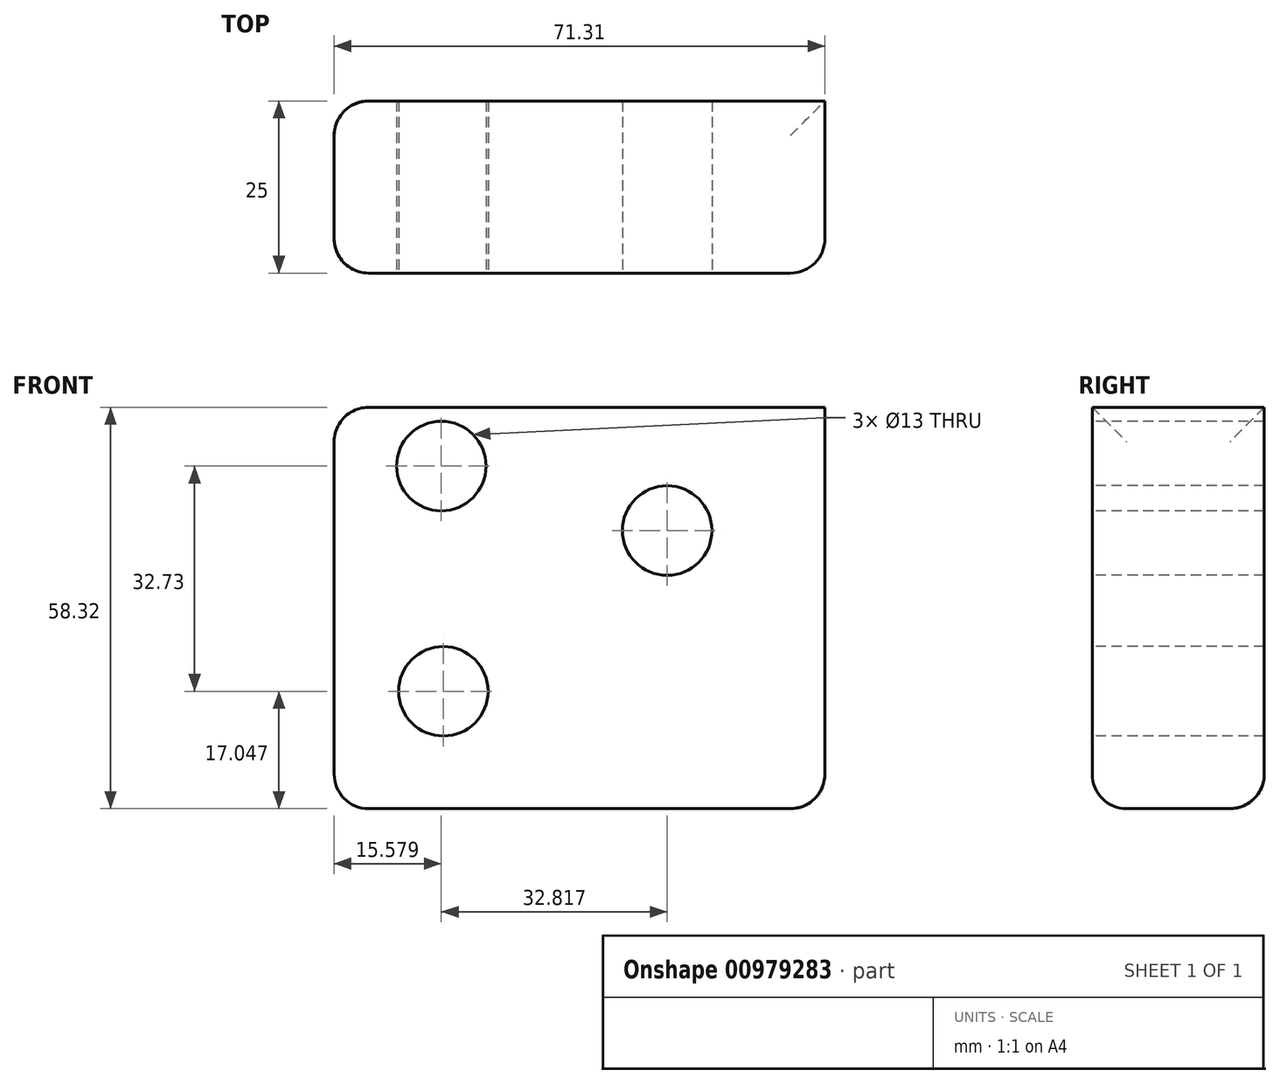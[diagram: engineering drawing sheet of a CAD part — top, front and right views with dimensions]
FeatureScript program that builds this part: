
annotation { "Feature Type Name" : "Feature", "Feature Type Description" : "" }
export const myFeature = defineFeature(function(context is Context, id is Id, definition is map)
    precondition{}
    {
        {
            var Q0;
            Q0=qCreatedBy(makeId("Front.planeOp"),FACE);
            var sketch = newSketch(context, id + "F0", { "sketchPlane" : qUnion([Q0])});
            skLineSegment(sketch, "E0.bottom", {"start": v(-136.04, 36.86) * mm, "end": v(-64.73, 36.86) * mm});
            skLineSegment(sketch, "E0.top", {"start": v(-136.04, -21.46) * mm, "end": v(-64.73, -21.46) * mm});
            skLineSegment(sketch, "E0.left", {"start": v(-136.04, 36.86) * mm, "end": v(-136.04, -21.46) * mm});
            skLineSegment(sketch, "E0.right", {"start": v(-64.73, 36.86) * mm, "end": v(-64.73, -21.46) * mm});
            skSolve(sketch);
        }
        {
            var Q0;
            Q0 = qSketchRegion(id + "F0", true);
            extrude(context, id + "F1", {"entities" : qUnion([Q0]), "depth" : 25 * mm, "offsetDistance" : 25 * mm});
        }
        {
            var Q0;
            Q0=makeQuery(id+"F1.opExtrude","CAP_FACE",FACE,{"disambiguationData":[OSD([sQuery(id+"F0.wireOp",EDGE,"E0.bottom"),sQuery(id+"F0.wireOp",EDGE,"E0.top"),sQuery(id+"F0.wireOp",EDGE,"E0.left"),sQuery(id+"F0.wireOp",EDGE,"E0.right")])],"isStart":false});
            var sketch = newSketch(context, id + "F2", { "sketchPlane" : qUnion([Q0])});
            skPoint(sketch, "E1", {"position": v(-120.46, 28.32) * mm});
            skPoint(sketch, "E2", {"position": v(-120.16, -4.41) * mm});
            skPoint(sketch, "E3", {"position": v(-87.64, 18.95) * mm});
            skSolve(sketch);
        }
        {
            var Q0;
            Q0=sQuery(id+"F2.wireOp",VERTEX,"E1");
            var Q1;
            Q1=sQuery(id+"F2.wireOp",VERTEX,"E2");
            var Q2;
            Q2=sQuery(id+"F2.wireOp",VERTEX,"E3");
            var Q3;
            Q3=makeQuery(id+"F1.opExtrude","SWEPT_BODY",BODY,{"disambiguationData":[OSD([sQuery(id+"F0.wireOp",EDGE,"E0.bottom"),sQuery(id+"F0.wireOp",EDGE,"E0.top"),sQuery(id+"F0.wireOp",EDGE,"E0.left"),sQuery(id+"F0.wireOp",EDGE,"E0.right")])]});
            hole(context, id + "F3", {"style" : HoleStyle.SIMPLE, "endStyle" : HoleEndStyle.BLIND, "holeDiameter" : 13 * mm, "majorDiameter" : 5 * mm, "holeDepth" : 51 * mm, "isTappedThrough" : true, "tappedDepth" : 12 * mm, "tapClearance" : 3, "startFromSketch" : true, "locations" : qUnion([Q0, Q1, Q2]), "scope" : qUnion([Q3])});
        }
        {
            var Q0;
            Q0=makeQuery(id+"F1.opExtrude","CAP_EDGE",EDGE,{"disambiguationData":[OSD([sQuery(id+"F0.wireOp",EDGE,"E0.right")])],"isStart":false});
            var Q1;
            Q1=makeQuery(id+"F1.opExtrude","CAP_EDGE",EDGE,{"disambiguationData":[OSD([sQuery(id+"F0.wireOp",EDGE,"E0.top")])],"isStart":false});
            var Q2;
            Q2=makeQuery(id+"F1.opExtrude","SWEPT_EDGE",EDGE,{"disambiguationData":[OSD([sQuery(id+"F0.wireOp",EDGE,"E0.top"),sQuery(id+"F0.wireOp",EDGE,"E0.left")])]});
            var Q3;
            Q3=makeQuery(id+"F1.opExtrude","SWEPT_FACE",FACE,{"disambiguationData":[OSD([sQuery(id+"F0.wireOp",EDGE,"E0.top")])]});
            var Q4;
            Q4=makeQuery(id+"F1.opExtrude","SWEPT_FACE",FACE,{"disambiguationData":[OSD([sQuery(id+"F0.wireOp",EDGE,"E0.left")])]});
            fillet(context, id + "F4", {"entities" : qUnion([Q0, Q1, Q2, Q3, Q4]), "tangentPropagation" : true, "radius" : 5 * mm, "defaultsChanged" : false, "vertexSettings" : [], "allowEdgeOverflow" : false});
        }
    });
